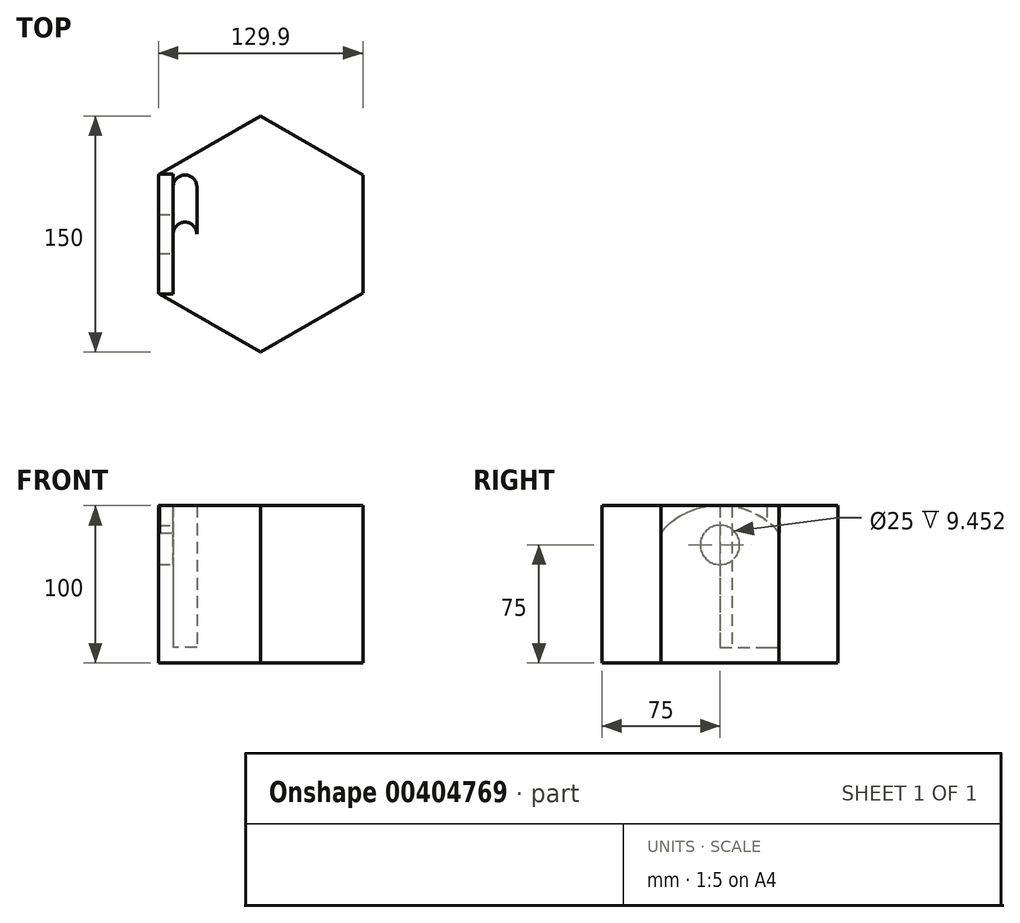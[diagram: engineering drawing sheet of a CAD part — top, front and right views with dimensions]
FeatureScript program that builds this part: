
annotation { "Feature Type Name" : "Feature", "Feature Type Description" : "" }
export const myFeature = defineFeature(function(context is Context, id is Id, definition is map)
    precondition{}
    {
        {
            var Q0;
            Q0=qCreatedBy(makeId("Top.planeOp"),FACE);
            var sketch = newSketch(context, id + "F0", { "sketchPlane" : qUnion([Q0])});
            skCircle(sketch, "E0.cCircle", {"center": v(0, 0) * mm, "radius": 75 * mm, "construction": true});
            skLineSegment(sketch, "E0.0", {"start": v(0, -75) * mm, "end": v(-64.95, -37.5) * mm});
            skLineSegment(sketch, "E0.1", {"start": v(-64.95, -37.5) * mm, "end": v(-64.95, 37.5) * mm});
            skLineSegment(sketch, "E0.2", {"start": v(-64.95, 37.5) * mm, "end": v(0, 75) * mm});
            skLineSegment(sketch, "E0.3", {"start": v(0, 75) * mm, "end": v(64.95, 37.5) * mm});
            skLineSegment(sketch, "E0.4", {"start": v(64.95, 37.5) * mm, "end": v(64.95, -37.5) * mm});
            skLineSegment(sketch, "E0.5", {"start": v(64.95, -37.5) * mm, "end": v(0, -75) * mm});
            skSolve(sketch);
        }
        {
            var Q0;
            Q0=makeQuery(id+"F0.imprint","IMPRINT",FACE,{"disambiguationData":[TD([[makeQuery(id+"F0.imprint","IMPRINT",EDGE,{"derivedFrom":sQuery(id+"F0.wireOp",EDGE,"E0.0")}),-1.0]])]});
            extrude(context, id + "F1", {"entities" : qUnion([Q0]), "depth" : 10 * mm});
        }
        {
            var Q0;
            Q0=makeQuery(id+"F1.opExtrude","CAP_FACE",FACE,{"disambiguationData":[OSD([sQuery(id+"F0.wireOp",EDGE,"E0.0"),sQuery(id+"F0.wireOp",EDGE,"E0.1"),sQuery(id+"F0.wireOp",EDGE,"E0.2"),sQuery(id+"F0.wireOp",EDGE,"E0.3"),sQuery(id+"F0.wireOp",EDGE,"E0.4"),sQuery(id+"F0.wireOp",EDGE,"E0.5")])],"isStart":false});
            var sketch = newSketch(context, id + "F2", { "sketchPlane" : qUnion([Q0])});
            skLineSegment(sketch, "E1", {"start": v(0, -75) * mm, "end": v(0, 75) * mm, "construction": true});
            skLineSegment(sketch, "E2", {"start": v(64.95, 0) * mm, "end": v(-64.95, 0) * mm, "construction": true});
            skPoint(sketch, "E3", {"position": v(-48, 0) * mm});
            skLineSegment(sketch, "E4", {"start": v(-48, 0) * mm, "end": v(-48, 30) * mm, "construction": true});
            skLineSegment(sketch, "E5.MirrorCS", {"start": v(-48, 0) * mm, "end": v(-48, -30) * mm, "construction": true});
            skArc(sketch, "E6.0.startCap", {"start": v(-40.5, 0) * mm, "mid": v(-48, -7.5) * mm, "end": v(-55.5, 0) * mm});
            skArc(sketch, "E6.0.endCap", {"start": v(-55.5, 30) * mm, "mid": v(-48, 37.5) * mm, "end": v(-40.5, 30) * mm});
            skLineSegment(sketch, "E6.0.left", {"start": v(-55.5, 0) * mm, "end": v(-55.5, 30) * mm});
            skLineSegment(sketch, "E6.0.right", {"start": v(-40.5, 0) * mm, "end": v(-40.5, 30) * mm});
            skArc(sketch, "E6.1.startCap", {"start": v(-55.5, 0) * mm, "mid": v(-48, 7.5) * mm, "end": v(-40.5, 0) * mm});
            skArc(sketch, "E6.1.endCap", {"start": v(-40.5, -30) * mm, "mid": v(-48, -37.5) * mm, "end": v(-55.5, -30) * mm});
            skLineSegment(sketch, "E6.1.left", {"start": v(-40.5, 0) * mm, "end": v(-40.5, -30) * mm});
            skLineSegment(sketch, "E6.1.right", {"start": v(-55.5, 0) * mm, "end": v(-55.5, -30) * mm});
            skSolve(sketch);
        }
        {
            var Q0;
            Q0=makeQuery(id+"F2.imprint","IMPRINT",FACE,{"disambiguationData":[TD([[makeQuery(id+"F2.imprint","IMPRINT",EDGE,{"derivedFrom":sQuery(id+"F2.wireOp",EDGE,"E6.0.startCap")}),1.0]])]});
            var Q1;
            Q1=makeQuery(id+"F2.imprint","IMPRINT",FACE,{"disambiguationData":[TD([[makeQuery(id+"F2.imprint","IMPRINT",EDGE,{"derivedFrom":sQuery(id+"F2.wireOp",EDGE,"E6.0.startCap")}),-1.0]])]});
            var Q2;
            Q2=makeQuery(id+"F2.imprint","IMPRINT",FACE,{"disambiguationData":[TD([[makeQuery(id+"F2.imprint","IMPRINT",EDGE,{"derivedFrom":sQuery(id+"F2.wireOp",EDGE,"E6.0.endCap")}),-1.0]])]});
            extrude(context, id + "F3", {"entities" : qUnion([Q0, Q1, Q2]), "operationType" : NewBodyOperationType.ADD, "depth" : 90 * mm});
        }
        {
            var Q0;
            Q0=makeQuery(id+"F3.opExtrude","SWEPT_FACE",FACE,{"disambiguationData":[OSD([sQuery(id+"F2.wireOp",EDGE,"E6.0.left"),sQuery(id+"F2.wireOp",EDGE,"E6.1.right")])]});
            var sketch = newSketch(context, id + "F4", { "sketchPlane" : qUnion([Q0])});
            skLineSegment(sketch, "E7", {"start": v(0, 0) * mm, "end": v(0, 100) * mm, "construction": true});
            skLineSegment(sketch, "E8.0", {"start": v(-38, 0) * mm, "end": v(-38, 50) * mm});
            skLineSegment(sketch, "E9.MirrorCS", {"start": v(38, 0) * mm, "end": v(38, 50) * mm});
            skCircle(sketch, "E10", {"center": v(0, 75) * mm, "radius": 12.5 * mm});
            skLineSegment(sketch, "E11", {"start": v(-38, 50) * mm, "end": v(38, 50) * mm, "construction": true});
            skArc(sketch, "E12.trimOffspring", {"start": v(38, 82.5) * mm, "mid": v(0, 100) * mm, "end": v(-38, 82.5) * mm});
            skLineSegment(sketch, "E13", {"start": v(-38, 100) * mm, "end": v(38, 100) * mm});
            skLineSegment(sketch, "E14.trimOffspring", {"start": v(-38, 82.5) * mm, "end": v(-38, 100) * mm});
            skLineSegment(sketch, "E15.trimOffspring", {"start": v(38, 82.5) * mm, "end": v(38, 100) * mm});
            skSolve(sketch);
        }
        {
            var Q0;
            {var subQ0=sQuery(id+"F4.wireOp",EDGE,"E14.trimOffspring");Q0=makeQuery(id+"F4.imprint","IMPRINT",FACE,{"disambiguationData":[TD([[makeQuery(id+"F4.imprint","IMPRINT",EDGE,{"derivedFrom":subQ0}),-1.0]])]});}
            var Q1;
            {var subQ0=sQuery(id+"F4.wireOp",EDGE,"E13");var subQ1=sQuery(id+"F4.wireOp",EDGE,"E12.trimOffspring");var subQ2=makeQuery(id+"F4.imprint","INTERSECT",VERTEX,{"derivedFrom":[subQ1,subQ0]});Q1=makeQuery(id+"F4.imprint","IMPRINT",FACE,{"disambiguationData":[TD([[makeQuery(id+"F4.imprint","IMPRINT",EDGE,{"disambiguationData":[TD([[subQ2,-1.0]])],"derivedFrom":subQ1}),-1.0]])]});}
            var Q2;
            {var subQ0=sQuery(id+"F4.wireOp",EDGE,"E13");var subQ1=sQuery(id+"F4.wireOp",EDGE,"E12.trimOffspring");var subQ2=makeQuery(id+"F4.imprint","INTERSECT",VERTEX,{"derivedFrom":[subQ1,subQ0]});Q2=makeQuery(id+"F4.imprint","IMPRINT",FACE,{"disambiguationData":[TD([[makeQuery(id+"F4.imprint","IMPRINT",EDGE,{"disambiguationData":[TD([[subQ2,1.0]])],"derivedFrom":subQ1}),-1.0]])]});}
            var Q3;
            {var subQ0=sQuery(id+"F4.wireOp",EDGE,"E15.trimOffspring");Q3=makeQuery(id+"F4.imprint","IMPRINT",FACE,{"disambiguationData":[TD([[makeQuery(id+"F4.imprint","IMPRINT",EDGE,{"derivedFrom":subQ0}),1.0]])]});}
            var Q4;
            Q4=makeQuery(id+"F4.imprint","IMPRINT",FACE,{"disambiguationData":[TD([[makeQuery(id+"F4.imprint","IMPRINT",EDGE,{"derivedFrom":sQuery(id+"F4.wireOp",EDGE,"E10")}),1.0]])]});
            var Q5;
            Q5=sQuery(id+"F4.wireOp",EDGE,"E14.trimOffspring");
            var Q6;
            Q6=sQuery(id+"F4.wireOp",EDGE,"E13");
            var Q7;
            Q7=sQuery(id+"F4.wireOp",EDGE,"E12.trimOffspring");
            var Q8;
            Q8=sQuery(id+"F4.wireOp",EDGE,"E15.trimOffspring");
            extrude(context, id + "F5", {"entities" : qUnion([Q0, Q1, Q2, Q3, Q4]), "operationType" : NewBodyOperationType.REMOVE, "surfaceEntities" : qUnion([Q5, Q6, Q7, Q8]), "endBound" : BoundingType.THROUGH_ALL, "oppositeDirection" : true, "depth" : 25 * mm});
        }
    });
